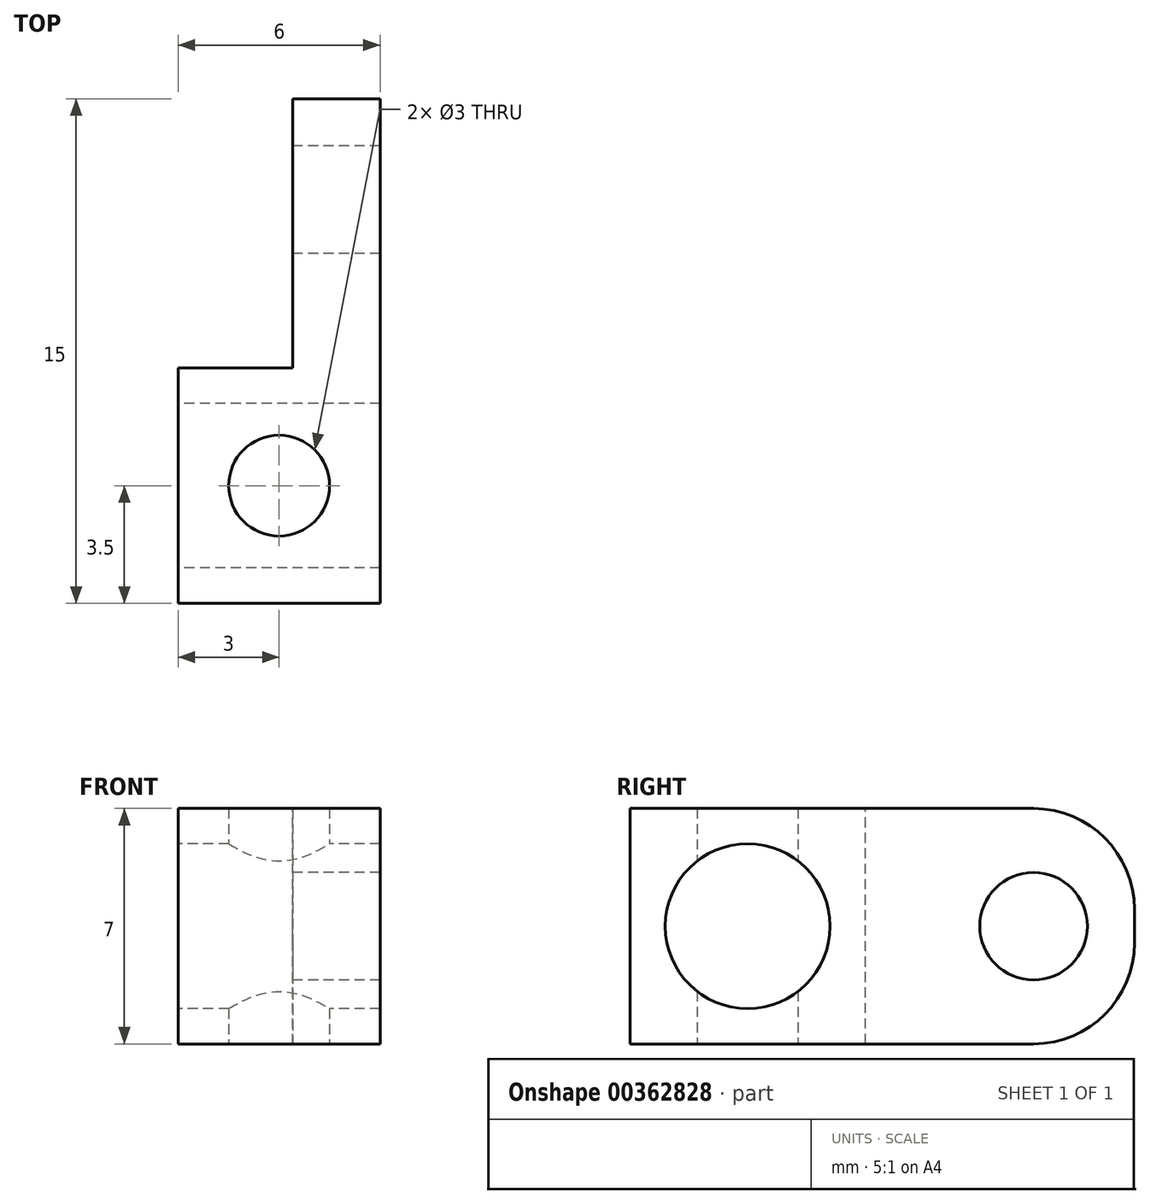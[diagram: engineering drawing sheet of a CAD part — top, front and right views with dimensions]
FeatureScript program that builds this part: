
annotation { "Feature Type Name" : "Feature", "Feature Type Description" : "" }
export const myFeature = defineFeature(function(context is Context, id is Id, definition is map)
    precondition{}
    {
        {
            var Q0;
            Q0=qCreatedBy(makeId("Top.planeOp"),FACE);
            var sketch = newSketch(context, id + "F0", { "sketchPlane" : qUnion([Q0])});
            skLineSegment(sketch, "E0.bottom", {"start": v(0, 0) * mm, "end": v(6, 0) * mm});
            skLineSegment(sketch, "E0.top", {"start": v(0, 15) * mm, "end": v(6, 15) * mm});
            skLineSegment(sketch, "E0.left", {"start": v(0, 0) * mm, "end": v(0, 15) * mm});
            skLineSegment(sketch, "E0.right", {"start": v(6, 0) * mm, "end": v(6, 15) * mm});
            skSolve(sketch);
        }
        {
            var Q0;
            Q0=makeQuery(id+"F0.imprint","IMPRINT",FACE,{"disambiguationData":[TD([[makeQuery(id+"F0.imprint","IMPRINT",EDGE,{"derivedFrom":sQuery(id+"F0.wireOp",EDGE,"E0.bottom")}),1.0]])]});
            extrude(context, id + "F1", {"entities" : qUnion([Q0]), "oppositeDirection" : true, "depth" : 7 * mm});
        }
        {
            var Q0;
            Q0=makeQuery(id+"F1.opExtrude","CAP_FACE",FACE,{"disambiguationData":[OSD([sQuery(id+"F0.wireOp",EDGE,"E0.bottom"),sQuery(id+"F0.wireOp",EDGE,"E0.top"),sQuery(id+"F0.wireOp",EDGE,"E0.left"),sQuery(id+"F0.wireOp",EDGE,"E0.right")])],"isStart":true});
            var sketch = newSketch(context, id + "F2", { "sketchPlane" : qUnion([Q0])});
            skLineSegment(sketch, "E1.bottom", {"start": v(0, 15) * mm, "end": v(3.4, 15) * mm});
            skLineSegment(sketch, "E1.top", {"start": v(0, 7) * mm, "end": v(3.4, 7) * mm});
            skLineSegment(sketch, "E1.left", {"start": v(0, 15) * mm, "end": v(0, 7) * mm});
            skLineSegment(sketch, "E1.right", {"start": v(3.4, 15) * mm, "end": v(3.4, 7) * mm});
            skSolve(sketch);
        }
        {
            var Q0;
            Q0=makeQuery(id+"F2.imprint","IMPRINT",FACE,{"disambiguationData":[TD([[makeQuery(id+"F2.imprint","IMPRINT",EDGE,{"derivedFrom":sQuery(id+"F2.wireOp",EDGE,"E1.bottom")}),-1.0]])]});
            extrude(context, id + "F3", {"entities" : qUnion([Q0]), "operationType" : NewBodyOperationType.REMOVE, "oppositeDirection" : true, "depth" : 25 * mm});
        }
        {
            var Q0;
            Q0=makeQuery(id+"F1.opExtrude","CAP_EDGE",EDGE,{"disambiguationData":[OSD([sQuery(id+"F0.wireOp",EDGE,"E0.top")])],"isStart":true});
            var Q1;
            Q1=makeQuery(id+"F1.opExtrude","CAP_EDGE",EDGE,{"disambiguationData":[OSD([sQuery(id+"F0.wireOp",EDGE,"E0.top")])],"isStart":false});
            fillet(context, id + "F4", {"entities" : qUnion([Q0, Q1]), "radius" : 3 * mm, "tangentPropagation" : true, "allowEdgeOverflow" : false});
        }
        {
            var Q0;
            Q0=makeQuery(id+"F1.opExtrude","SWEPT_FACE",FACE,{"disambiguationData":[OSD([sQuery(id+"F0.wireOp",EDGE,"E0.left")])]});
            var sketch = newSketch(context, id + "F5", { "sketchPlane" : qUnion([Q0])});
            skCircle(sketch, "E2", {"center": v(-3.5, -3.5) * mm, "radius": 2.45 * mm});
            skSolve(sketch);
        }
        {
            var Q0;
            Q0=makeQuery(id+"F5.imprint","IMPRINT",FACE,{"disambiguationData":[TD([[makeQuery(id+"F5.imprint","IMPRINT",EDGE,{"derivedFrom":sQuery(id+"F5.wireOp",EDGE,"E2")}),1.0]])]});
            extrude(context, id + "F6", {"entities" : qUnion([Q0]), "operationType" : NewBodyOperationType.REMOVE, "oppositeDirection" : true, "depth" : 25 * mm});
        }
        {
            var Q0;
            Q0=makeQuery(id+"F3.boolean.opBoolean","COPY",FACE,{"derivedFrom":makeQuery(id+"F3.opExtrude","SWEPT_FACE",FACE,{"disambiguationData":[OSD([sQuery(id+"F2.wireOp",EDGE,"E1.right")])]})});
            var sketch = newSketch(context, id + "F7", { "sketchPlane" : qUnion([Q0])});
            skCircle(sketch, "E3", {"center": v(-12, -3.5) * mm, "radius": 1.6 * mm});
            skSolve(sketch);
        }
        {
            var Q0;
            Q0 = qSketchRegion(id + "F7", true);
            extrude(context, id + "F8", {"entities" : qUnion([Q0]), "operationType" : NewBodyOperationType.REMOVE, "oppositeDirection" : true, "depth" : 25 * mm});
        }
        {
            var Q0;
            Q0=makeQuery(id+"F1.opExtrude","CAP_FACE",FACE,{"disambiguationData":[OSD([sQuery(id+"F0.wireOp",EDGE,"E0.bottom"),sQuery(id+"F0.wireOp",EDGE,"E0.top"),sQuery(id+"F0.wireOp",EDGE,"E0.left"),sQuery(id+"F0.wireOp",EDGE,"E0.right")])],"isStart":false});
            var sketch = newSketch(context, id + "F9", { "sketchPlane" : qUnion([Q0])});
            skCircle(sketch, "E4", {"center": v(3, -3.5) * mm, "radius": 1.5 * mm});
            skSolve(sketch);
        }
        {
            var Q0;
            Q0 = qSketchRegion(id + "F9", true);
            extrude(context, id + "F10", {"entities" : qUnion([Q0]), "operationType" : NewBodyOperationType.REMOVE, "oppositeDirection" : true, "depth" : 25 * mm});
        }
    });
